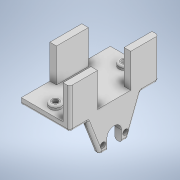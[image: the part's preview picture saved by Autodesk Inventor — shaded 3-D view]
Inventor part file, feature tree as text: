
AUTODESK INVENTOR PART (.ipt)
format: ipt  version: 2020 (Build 240168000, 168)  size: 277,504 bytes
history: native  units: in
note: dims shown in document units (in); Inventor stores cm internally (conversion verified against a paired STEP export)
features: extrude x8, sketch x7, fillet x5
ambient origin geometry x8: Origin, YZ Plane, XZ Plane, XY Plane, X Axis, Y Axis, Z Axis, Center Point
bodies: Solid1 (feature_tree)
feature tree (20):
  extrude  "Extrusion1"  Depth=2.6378in
  extrude  "Extrusion2"  Depth=0.1969in
  extrude  "Extrusion3"  Depth=0.1969in
  extrude  "Extrusion4"  Depth=1.0in TaperAngle=0.0deg
  extrude  "Extrusion5"  Depth=0.3346in
  fillet  "Fillet1"  Radius=0.3346in
  fillet  "Fillet2"  Radius=0.1181in
  extrude  "Extrusion6"  Depth=0.2362in
  extrude  "Extrusion7"  Depth=0.0783in
  extrude  "Extrusion8"  Depth=0.0783in
  fillet  "Fillet3"  Radius=0.5906in
  fillet  "Fillet4"  Radius=0.0591in
  fillet  "Fillet5"  Radius=0.0787in
  sketch  "Sketch1"  dims[d0=1.4331in d1=2.6378in]
  sketch  "Sketch2"  dims[d2=0.1969in d3=0.0in d4=0.1969in]
  sketch  "Sketch3"  dims[d5=0.8268in d6=0.1969in]
  sketch  "Sketch4"  dims[d7=0.8268in d8=1.0in d9=0.0in]
  sketch  "Sketch6"  dims[d10=0.3346in d11=0.3346in d12=0.3346in d13=0.1181in d14=0.0in]
  sketch  "Sketch7"  dims[d15=0.2362in d16=0.2362in]
  sketch  "Sketch8"  dims[d17=0.1181in d18=0.0in d19=0.1575in d21=0.1575in d22=0.5906in d23=0.0in d24=0.0591in d25=0.0787in d26=0.1969in d27=0.9449in d28=1.0in d29=0.0in d30=0.7165in d31=0.7165in d32=0.1575in d33=1.6142in d34=1.0157in d35=0.1969in d36=0.0in d37=0.0in d38=0.1575in d39=0.1575in d40=0.4331in d41=0.5512in d42=1.0157in d43=0.0in d44=0.2165in d45=0.0783in d46=0.0783in]
